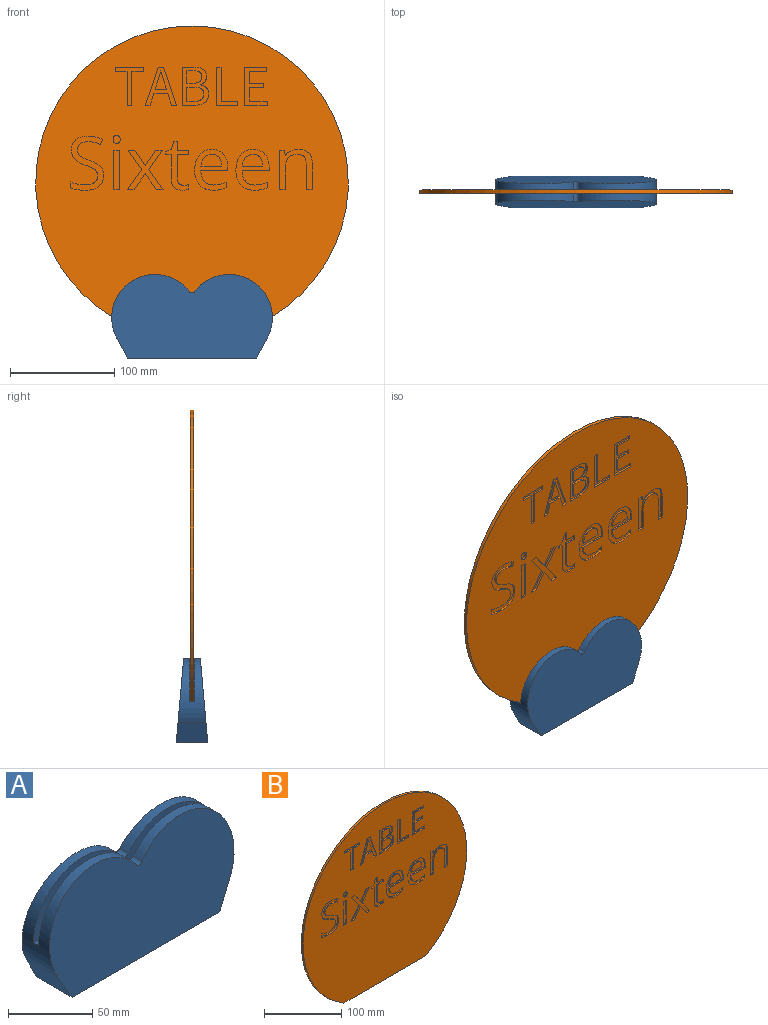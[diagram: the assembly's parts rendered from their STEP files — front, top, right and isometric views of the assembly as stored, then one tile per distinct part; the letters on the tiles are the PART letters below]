
ASSEMBLY  parts=2 mates=1
PART A: 67 faces, bbox 154.2x30x80.1 mm
  f0: plane 101.83x38.65mm, normal (0,-1,0), area 2079.1mm2, adj f5,f6,f9,f22,f25,f36,f37,f39
  f1: plane 101.83x38.65mm, normal (0,1,0), area 2079.1mm2, adj f2,f5,f6,f7,f21,f24,f26,f37
  f2: plane 14x1.74mm, normal (-1,0,0), area 24.3mm2, adj f1,f3,f38,f46
  f3: plane 16.17x14mm, normal (0,1,0), area 226.4mm2, adj f2,f38,f46,f61
  f4: plane 14x13.34mm, normal (0,-1,0), area 186.7mm2, adj f39,f40,f60,f62
  f5: plane 123.75x30mm, normal (0,0,-1), area 1755.7mm2, adj f0,f1,f12,f15,f16,f17,f23,f26
  f6: plane 35.45x10.65mm, normal (1,0,0), area 364.4mm2, adj f0,f1,f20,f21,f22,f24,f25,f37
  f7: plane 23.8x0.56mm, normal (-1,0,0), area 13.4mm2, adj f1,f24,f37,f55
  f8: plane 45.65x23.8mm, normal (0,1,0), area 1086.5mm2, adj f24,f37,f54,f55
  f9: plane 23.8x0.56mm, normal (-1,0,0), area 13.4mm2, adj f0,f25,f37,f53
  f10: plane 45.65x23.8mm, normal (0,-1,0), area 1086.5mm2, adj f25,f37,f52,f53
  f11: plane 24.61x4mm, normal (0,0,1), area 98.3mm2, adj f13,f18,f19,f23,f63,f64
  f12: plane 30x18.92mm, normal (0.88,0,-0.48), area 609.5mm2, adj f5,f13,f16,f17
  f13: cylinder r=41.5mm len=74.56mm, axis (0,1,0), area 1962.3mm2, adj f11,f12,f16,f17,f18,f19,f65,f66
  f14: cylinder r=41.5mm len=74.56mm, axis (0,1,0), area 1962.3mm2, adj f15,f16,f17,f18,f19,f20,f65,f66
  f15: plane 30x18.92mm, normal (-0.88,0,-0.48), area 609.5mm2, adj f5,f14,f16,f17
  f16: plane 154.17x80.15mm, normal (0,-1,0.09), area 10797.1mm2, adj f5,f12,f13,f14,f15,f66
  f17: plane 154.17x80.15mm, normal (0,1,0.09), area 10797.1mm2, adj f5,f12,f13,f14,f15,f65
  f18: plane 154.17x41.5mm, normal (0,1,0), area 5244.2mm2, adj f11,f13,f14,f20,f21,f66
  f19: plane 154.17x41.5mm, normal (0,-1,0), area 5244.2mm2, adj f11,f13,f14,f20,f22,f65
  f20: plane 24.58x4mm, normal (0,0,1), area 98.3mm2, adj f6,f14,f18,f19
  f21: plane 104.97x2.76mm, normal (0,0,-1), area 287.9mm2, adj f1,f6,f18,f64
  f22: plane 104.97x2.76mm, normal (0,0,-1), area 287.9mm2, adj f0,f6,f19,f63
  f23: plane 38.65x3.18mm, normal (-1,0,0), area 122.7mm2, adj f5,f11,f63,f64
  f24: plane 52x3.74mm, normal (0,0,-1), area 190mm2, adj f1,f6,f7,f8,f54,f55
  f25: plane 52x3.74mm, normal (0,0,-1), area 190mm2, adj f0,f6,f9,f10,f52,f53
  f26: extruded ~3.2x0.47mm, area 1.6mm2, adj f1,f5,f27,f37
  f27: plane 3.2x3.09mm, normal (-1,0,0), area 9.9mm2, adj f5,f26,f37,f48
  f28: plane 51.65x3.2mm, normal (0,1,0), area 165.3mm2, adj f5,f37,f48,f49
  f29: plane 3.2x3.09mm, normal (1,0,0), area 9.9mm2, adj f5,f30,f37,f49
  f30: extruded ~3.2x2.74mm, area 13mm2, adj f5,f29,f31,f37
  f31: cylinder r=2.5mm len=5mm, axis (0,0,-1), area 25.1mm2, adj f5,f30,f32,f37
  f32: extruded ~3.2x2.74mm, area 13mm2, adj f5,f31,f33,f37
  f33: plane 3.2x3.09mm, normal (1,0,0), area 9.9mm2, adj f5,f32,f37,f51
  f34: plane 51.65x3.2mm, normal (0,-1,0), area 165.3mm2, adj f5,f37,f50,f51
  f35: plane 3.2x3.09mm, normal (-1,0,0), area 9.9mm2, adj f5,f36,f37,f50
  f36: extruded ~3.2x0.47mm, area 1.6mm2, adj f0,f5,f35,f37
  f37: plane 63.11x23mm, normal (0,0,-1), area 447.2mm2, adj f0,f1,f6,f7,f8,f9,f10,f26
  f38: plane 19x1.74mm, normal (0,0,-1), area 31.6mm2, adj f1,f2,f3,f61
  f39: plane 19x1.74mm, normal (0,0,-1), area 30.2mm2, adj f0,f4,f60,f62
  f40: plane 22x3.24mm, normal (0,0,-1), area 36.7mm2, adj f0,f4,f41,f42,f43,f57,f58,f60
  f41: plane 15.65x8mm, normal (0,-1,0), area 125.2mm2, adj f5,f40,f57,f58
  f42: plane 8x0.06mm, normal (-1,0,0), area 0.5mm2, adj f0,f5,f40,f57
  f43: plane 8x0.06mm, normal (1,0,0), area 0.5mm2, adj f0,f5,f40,f58
  f44: plane 8x0.06mm, normal (1,0,0), area 0.5mm2, adj f1,f5,f46,f59
  f45: plane 8x0.06mm, normal (-1,0,0), area 0.5mm2, adj f1,f5,f46,f56
  f46: plane 22x3.24mm, normal (0,0,-1), area 35.3mm2, adj f1,f2,f3,f44,f45,f47,f56,f59
  f47: plane 15.65x8mm, normal (0,1,0), area 125.2mm2, adj f5,f46,f56,f59
  f48: cylinder r=3.17mm len=3.2mm, axis (0,0,1), area 16mm2, adj f5,f27,f28,f37
  f49: cylinder r=3.17mm len=3.2mm, axis (0,0,-1), area 16mm2, adj f5,f28,f29,f37
  f50: cylinder r=3.17mm len=3.2mm, axis (0,0,-1), area 16mm2, adj f5,f34,f35,f37
  f51: cylinder r=3.17mm len=3.2mm, axis (0,0,1), area 16mm2, adj f5,f33,f34,f37
  f52: cylinder r=3.17mm len=23.8mm, axis (0,0,1), area 118.7mm2, adj f6,f10,f25,f37
  f53: cylinder r=3.17mm len=23.8mm, axis (0,0,1), area 118.7mm2, adj f9,f10,f25,f37
  f54: cylinder r=3.17mm len=23.8mm, axis (0,0,-1), area 118.7mm2, adj f6,f8,f24,f37
  f55: cylinder r=3.17mm len=23.8mm, axis (0,0,-1), area 118.7mm2, adj f7,f8,f24,f37
  f56: cylinder r=3.17mm len=8mm, axis (0,0,1), area 39.9mm2, adj f5,f45,f46,f47
  f57: cylinder r=3.17mm len=8mm, axis (0,0,-1), area 39.9mm2, adj f5,f40,f41,f42
  f58: cylinder r=3.17mm len=8mm, axis (0,0,1), area 39.9mm2, adj f5,f40,f41,f43
  f59: cylinder r=3.17mm len=8mm, axis (0,0,-1), area 39.9mm2, adj f5,f44,f46,f47
  f60: cylinder r=3.17mm len=14mm, axis (0,0,-1), area 48.9mm2, adj f0,f4,f39,f40
  f61: cylinder r=3.17mm len=14mm, axis (0,0,-1), area 48.9mm2, adj f1,f3,f38,f46
  f62: cylinder r=3.17mm len=14mm, axis (0,0,-1), area 48.9mm2, adj f0,f4,f39,f40
  f63: cylinder r=3.17mm len=38.65mm, axis (0,0,-1), area 192.7mm2, adj f0,f5,f11,f22,f23
  f64: cylinder r=3.17mm len=38.65mm, axis (0,0,1), area 192.7mm2, adj f1,f5,f11,f21,f23
  f65: cylinder r=3.17mm len=7.53mm, axis (0,-1,0), area 43.9mm2, adj f13,f14,f17,f19
  f66: cylinder r=3.17mm len=7.53mm, axis (0,-1,0), area 43.9mm2, adj f13,f14,f16,f18
PART B: 203 faces, bbox 300x3.2x279.9 mm
  f0: plane 300x279.9mm, normal (0,-1,0), area 62829.4mm2, adj f1,f3,f4,f5,f6,f7,f8,f9
  f1: cylinder r=150mm len=300mm, axis (0,1,0), area 2493.6mm2, adj f0,f2,f3
  f2: plane 300x279.9mm, normal (0,1,0), area 68647.6mm2, adj f1,f3
  f3: plane 150x3.18mm, normal (0,0,-1), area 476.2mm2, adj f0,f1,f2
  f4: plane 32.8x2mm, normal (1,0,0), area 65.6mm2, adj f0,f5,f11,f12
  f5: plane 4.66x2mm, normal (0,0,1), area 9.3mm2, adj f0,f4,f6,f12
  f6: plane 32.8x2mm, normal (-1,0,0), area 65.6mm2, adj f0,f5,f7,f12
  f7: plane 11.12x2mm, normal (0,0,1), area 22.2mm2, adj f0,f6,f8,f12
  f8: plane 3.9x2mm, normal (-1,0,0), area 7.8mm2, adj f0,f7,f9,f12
  f9: plane 26.9x2mm, normal (0,0,-1), area 53.8mm2, adj f0,f8,f10,f12
  f10: plane 3.9x2mm, normal (1,0,0), area 7.8mm2, adj f0,f9,f11,f12
  f11: plane 11.12x2mm, normal (0,0,1), area 22.2mm2, adj f0,f4,f10,f12
  f12: plane 36.71x26.9mm, normal (0,-1,0), area 257.7mm2, adj f4,f5,f6,f7,f8,f9,f10,f11
  f13: plane 11.12x2mm, normal (0,0,-1), area 22.2mm2, adj f14,f26,f27,f200
  f14: plane 5.61x2mm, normal (-0.95,0,0.31), area 11.8mm2, adj f13,f15,f27,f200
  f15: extruded ~12.42x3.65mm, area 25.9mm2, adj f14,f16,f27,f200
  f16: plane 2x0.2mm, normal (0,0,1), area 0.4mm2, adj f15,f17,f27,f200
  f17: extruded ~12.42x3.7mm, area 25.9mm2, adj f16,f26,f27,f200
  f18: plane 11.22x3.51mm, normal (0.95,0,0.3), area 23.5mm2, adj f0,f19,f25,f27
  f19: plane 4.91x2mm, normal (0,0,1), area 9.8mm2, adj f0,f18,f20,f27
  f20: plane 36.71x12.47mm, normal (-0.95,0,-0.32), area 77.5mm2, adj f0,f19,f21,f27
  f21: plane 5.16x2mm, normal (0,0,-1), area 10.3mm2, adj f0,f20,f22,f27
  f22: plane 36.71x12.47mm, normal (0.95,0,-0.32), area 77.5mm2, adj f0,f21,f23,f27
  f23: plane 4.71x2mm, normal (0,0,1), area 9.4mm2, adj f0,f22,f24,f27
  f24: plane 11.22x3.55mm, normal (-0.95,0,0.3), area 23.5mm2, adj f0,f23,f25,f27
  f25: plane 13.42x2mm, normal (0,0,1), area 26.8mm2, adj f0,f18,f24,f27
  f26: plane 5.61x2mm, normal (0.95,0,0.3), area 11.8mm2, adj f13,f17,f27,f200
  f27: plane 36.71x30.1mm, normal (0,-1,0), area 357.5mm2, adj f13,f14,f15,f16,f17,f18,f19,f20
  f28: extruded ~7.25x2.96mm, area 16.2mm2, adj f29,f46,f47,f201
  f29: extruded ~6.9x2.88mm, area 15.5mm2, adj f28,f30,f47,f201
  f30: extruded ~8.29x2.41mm, area 17.6mm2, adj f29,f31,f47,f201
  f31: plane 19.76x2mm, normal (0,0,-1), area 39.5mm2, adj f30,f46,f47,f201
  f32: extruded ~13.22x5.11mm, area 29.2mm2, adj f0,f33,f45,f47
  f33: extruded ~6.53x2mm, area 13.1mm2, adj f0,f32,f34,f47
  f34: extruded ~5.74x2mm, area 12.1mm2, adj f0,f33,f35,f47
  f35: plane 5.11x2mm, normal (-1,0,0), area 10.2mm2, adj f0,f34,f36,f47
  f36: extruded ~12.06x2.55mm, area 24.8mm2, adj f0,f35,f37,f47
  f37: extruded ~8.98x3.45mm, area 19.8mm2, adj f0,f36,f38,f47
  f38: extruded ~10.1x3.37mm, area 21.8mm2, adj f0,f37,f39,f47
  f39: plane 26.03x2mm, normal (0,0,1), area 52.1mm2, adj f0,f38,f40,f47
  f40: plane 3.62x2mm, normal (-1,0,0), area 7.2mm2, adj f0,f39,f41,f47
  f41: extruded ~12.33x4.14mm, area 26.6mm2, adj f0,f40,f42,f47
  f42: extruded ~11.23x4.67mm, area 25.1mm2, adj f0,f41,f43,f47
  f43: extruded ~12.09x5.38mm, area 27.4mm2, adj f0,f42,f44,f47
  f44: extruded ~14.52x4.5mm, area 31.1mm2, adj f0,f43,f45,f47
  f45: extruded ~14.17x4.85mm, area 30.7mm2, adj f0,f32,f44,f47
  f46: extruded ~8.2x3.19mm, area 17.9mm2, adj f28,f31,f47,f201
  f47: plane 39.18x31.96mm, normal (0,-1,0), area 569.5mm2, adj f28,f29,f30,f31,f32,f33,f34,f35
  f48: extruded ~7.25x2.96mm, area 16.2mm2, adj f49,f66,f67,f202
  f49: extruded ~6.9x2.88mm, area 15.5mm2, adj f48,f50,f67,f202
  f50: extruded ~8.29x2.41mm, area 17.6mm2, adj f49,f51,f67,f202
  f51: plane 19.76x2mm, normal (0,0,-1), area 39.5mm2, adj f50,f66,f67,f202
  f52: extruded ~13.22x5.11mm, area 29.2mm2, adj f0,f53,f65,f67
  f53: extruded ~6.53x2mm, area 13.1mm2, adj f0,f52,f54,f67
  f54: extruded ~5.74x2mm, area 12.1mm2, adj f0,f53,f55,f67
  f55: plane 5.11x2mm, normal (-1,0,0), area 10.2mm2, adj f0,f54,f56,f67
  f56: extruded ~12.06x2.55mm, area 24.8mm2, adj f0,f55,f57,f67
  f57: extruded ~8.98x3.45mm, area 19.8mm2, adj f0,f56,f58,f67
  f58: extruded ~10.1x3.37mm, area 21.8mm2, adj f0,f57,f59,f67
  f59: plane 26.03x2mm, normal (0,0,1), area 52.1mm2, adj f0,f58,f60,f67
  f60: plane 3.62x2mm, normal (-1,0,0), area 7.2mm2, adj f0,f59,f61,f67
  f61: extruded ~12.33x4.14mm, area 26.6mm2, adj f0,f60,f62,f67
  f62: extruded ~11.23x4.67mm, area 25.1mm2, adj f0,f61,f63,f67
  f63: extruded ~12.09x5.38mm, area 27.4mm2, adj f0,f62,f64,f67
  f64: extruded ~14.52x4.5mm, area 31.1mm2, adj f0,f63,f65,f67
  f65: extruded ~14.17x4.85mm, area 30.7mm2, adj f0,f52,f64,f67
  f66: extruded ~8.2x3.19mm, area 17.9mm2, adj f48,f51,f67,f202
  f67: plane 39.18x31.96mm, normal (0,-1,0), area 569.5mm2, adj f48,f49,f50,f51,f52,f53,f54,f55
  f68: plane 36.71x2mm, normal (1,0,0), area 73.4mm2, adj f0,f69,f85,f86
  f69: plane 11.72x2mm, normal (0,0,1), area 23.4mm2, adj f0,f68,f70,f86
  f70: extruded ~13.92x10.77mm, area 39.8mm2, adj f0,f69,f71,f86
  f71: extruded ~8.76x7.51mm, area 25.3mm2, adj f0,f70,f72,f86
  f72: plane 2x0.25mm, normal (-1,0,0), area 0.5mm2, adj f0,f71,f73,f86
  f73: extruded ~7.97x5.41mm, area 20.6mm2, adj f0,f72,f74,f86
  f74: extruded ~12.62x8.96mm, area 35.1mm2, adj f0,f73,f85,f86
  f75: plane 6.41x2mm, normal (0,0,-1), area 12.8mm2, adj f76,f83,f86,f88
  f76: plane 13.82x2mm, normal (-1,0,0), area 27.6mm2, adj f75,f77,f86,f88
  f77: plane 6.41x2mm, normal (0,0,1), area 12.8mm2, adj f76,f78,f86,f88
  f78: extruded ~10.02x6.61mm, area 27.2mm2, adj f77,f83,f86,f88
  f79: plane 5.46x2mm, normal (0,0,-1), area 10.9mm2, adj f80,f84,f86,f87
  f80: plane 11.97x2mm, normal (-1,0,0), area 23.9mm2, adj f79,f81,f86,f87
  f81: plane 5.66x2mm, normal (0,0,1), area 11.3mm2, adj f80,f82,f86,f87
  f82: extruded ~8.67x5.91mm, area 24mm2, adj f81,f84,f86,f87
  f83: extruded ~10.02x7.21mm, area 28mm2, adj f75,f78,f86,f88
  f84: extruded ~8.87x6.06mm, area 24.4mm2, adj f79,f82,f86,f87
  f85: plane 10.92x2mm, normal (0,0,-1), area 21.8mm2, adj f0,f68,f74,f86
  f86: plane 36.71x25.64mm, normal (0,-1,0), area 472.9mm2, adj f68,f69,f70,f71,f72,f73,f74,f75
  f87: plane 14.33x11.97mm, normal (0,-1,0), area 154.5mm2, adj f79,f80,f81,f82,f84
  f88: plane 16.43x13.82mm, normal (0,-1,0), area 203.7mm2, adj f75,f76,f77,f78,f83
  f89: plane 36.71x2mm, normal (1,0,0), area 73.4mm2, adj f0,f90,f94,f95
  f90: plane 20.68x2mm, normal (0,0,1), area 41.4mm2, adj f0,f89,f91,f95
  f91: plane 3.96x2mm, normal (-1,0,0), area 7.9mm2, adj f0,f90,f92,f95
  f92: plane 16.03x2mm, normal (0,0,-1), area 32.1mm2, adj f0,f91,f93,f95
  f93: plane 32.75x2mm, normal (-1,0,0), area 65.5mm2, adj f0,f92,f94,f95
  f94: plane 4.66x2mm, normal (0,0,-1), area 9.3mm2, adj f0,f89,f93,f95
  f95: plane 36.71x20.68mm, normal (0,-1,0), area 234.4mm2, adj f89,f90,f91,f92,f93,f94
  f96: plane 36.71x2mm, normal (1,0,0), area 73.4mm2, adj f0,f97,f107,f108
  f97: plane 21.74x2mm, normal (0,0,1), area 43.5mm2, adj f0,f96,f98,f108
  f98: plane 3.96x2mm, normal (-1,0,0), area 7.9mm2, adj f0,f97,f99,f108
  f99: plane 17.08x2mm, normal (0,0,-1), area 34.2mm2, adj f0,f98,f100,f108
  f100: plane 13.37x2mm, normal (-1,0,0), area 26.7mm2, adj f0,f99,f101,f108
  f101: plane 13.92x2mm, normal (0,0,1), area 27.8mm2, adj f0,f100,f102,f108
  f102: plane 3.96x2mm, normal (-1,0,0), area 7.9mm2, adj f0,f101,f103,f108
  f103: plane 13.92x2mm, normal (0,0,-1), area 27.8mm2, adj f0,f102,f104,f108
  f104: plane 11.52x2mm, normal (-1,0,0), area 23mm2, adj f0,f103,f105,f108
  f105: plane 16.53x2mm, normal (0,0,1), area 33.1mm2, adj f0,f104,f106,f108
  f106: plane 3.9x2mm, normal (-1,0,0), area 7.8mm2, adj f0,f105,f107,f108
  f107: plane 21.18x2mm, normal (0,0,-1), area 42.4mm2, adj f0,f96,f106,f108
  f108: plane 36.71x21.74mm, normal (0,-1,0), area 358.2mm2, adj f96,f97,f98,f99,f100,f101,f102,f103
  f109: extruded ~10.38x4.83mm, area 23.8mm2, adj f0,f110,f133,f134
  f110: extruded ~8.41x2.98mm, area 18.3mm2, adj f0,f109,f111,f134
  f111: extruded ~10.91x6.07mm, area 25.2mm2, adj f0,f110,f112,f134
  f112: extruded ~7.02x3.08mm, area 15.4mm2, adj f0,f111,f113,f134
  f113: extruded ~3.26x3.07mm, area 9.1mm2, adj f0,f112,f114,f134
  f114: extruded ~4.29x2mm, area 8.9mm2, adj f0,f113,f115,f134
  f115: extruded ~5.55x2.62mm, area 12.8mm2, adj f0,f114,f116,f134
  f116: extruded ~7.28x2mm, area 15.4mm2, adj f0,f115,f117,f134
  f117: extruded ~12.14x2.61mm, area 25mm2, adj f0,f116,f118,f134
  f118: plane 5.1x2mm, normal (-0.94,0,0.34), area 10.8mm2, adj f0,f117,f119,f134
  f119: extruded ~13.82x2.76mm, area 28.4mm2, adj f0,f118,f120,f134
  f120: extruded ~11.59x3.45mm, area 24.6mm2, adj f0,f119,f121,f134
  f121: extruded ~9.27x4.37mm, area 21.3mm2, adj f0,f120,f122,f134
  f122: extruded ~9x3.02mm, area 19.4mm2, adj f0,f121,f123,f134
  f123: extruded ~10.05x5.96mm, area 23.6mm2, adj f0,f122,f124,f134
  f124: extruded ~7.5x3.21mm, area 16.3mm2, adj f0,f123,f125,f134
  f125: extruded ~3.52x3.09mm, area 9.5mm2, adj f0,f124,f126,f134
  f126: extruded ~4.29x2mm, area 8.9mm2, adj f0,f125,f127,f134
  f127: extruded ~6.19x2.97mm, area 14.3mm2, adj f0,f126,f128,f134
  f128: extruded ~8.83x2.22mm, area 18.5mm2, adj f0,f127,f129,f134
  f129: extruded ~7.24x2mm, area 14.6mm2, adj f0,f128,f130,f134
  f130: extruded ~6.76x2.06mm, area 14.2mm2, adj f0,f129,f131,f134
  f131: plane 5.65x2mm, normal (1,0,0), area 11.3mm2, adj f0,f130,f132,f134
  f132: extruded ~13.79x2.32mm, area 28.2mm2, adj f0,f131,f133,f134
  f133: extruded ~13.1x3.73mm, area 27.7mm2, adj f0,f109,f132,f134
  f134: plane 51.82x31.72mm, normal (0,-1,0), area 588.1mm2, adj f109,f110,f111,f112,f113,f114,f115,f116
  f135: plane 5.73x2mm, normal (0,0,1), area 11.5mm2, adj f0,f136,f138,f139
  f136: plane 37.79x2mm, normal (-1,0,0), area 75.6mm2, adj f0,f135,f137,f139
  f137: plane 5.73x2mm, normal (0,0,-1), area 11.5mm2, adj f0,f136,f138,f139
  f138: plane 37.79x2mm, normal (1,0,0), area 75.6mm2, adj f0,f135,f137,f139
  f139: plane 37.79x5.73mm, normal (0,-1,0), area 216.4mm2, adj f135,f136,f137,f138
  f140: extruded ~2.88x2mm, area 6.2mm2, adj f0,f141,f147,f148
  f141: extruded ~2.88x2mm, area 6.2mm2, adj f0,f140,f142,f148
  f142: extruded ~2.42x2mm, area 5.3mm2, adj f0,f141,f143,f148
  f143: extruded ~2.38x2mm, area 5.3mm2, adj f0,f142,f144,f148
  f144: extruded ~2.88x2mm, area 6.3mm2, adj f0,f143,f145,f148
  f145: extruded ~2.86x2mm, area 6.2mm2, adj f0,f144,f146,f148
  f146: extruded ~2.38x2mm, area 5.2mm2, adj f0,f145,f147,f148
  f147: extruded ~2.42x2mm, area 5.3mm2, adj f0,f140,f146,f148
  f148: plane 7.62x6.76mm, normal (0,-1,0), area 42mm2, adj f140,f141,f142,f143,f144,f145,f146,f147
  f149: plane 18.45x13.14mm, normal (0.81,0,0.58), area 45.3mm2, adj f0,f150,f160,f161
  f150: plane 19.34x13.82mm, normal (0.81,0,-0.58), area 47.5mm2, adj f0,f149,f151,f161
  f151: plane 6.48x2mm, normal (0,0,1), area 13mm2, adj f0,f150,f152,f161
  f152: plane 15.31x10.69mm, normal (-0.82,0,0.57), area 37.4mm2, adj f0,f151,f153,f161
  f153: plane 15.31x10.59mm, normal (0.82,0,0.57), area 37.2mm2, adj f0,f152,f154,f161
  f154: plane 6.48x2mm, normal (0,0,1), area 13mm2, adj f0,f153,f155,f161
  f155: plane 19.34x13.82mm, normal (-0.81,0,-0.58), area 47.5mm2, adj f0,f154,f156,f161
  f156: plane 18.45x13.14mm, normal (-0.81,0,0.58), area 45.3mm2, adj f0,f155,f157,f161
  f157: plane 6.45x2mm, normal (0,0,-1), area 12.9mm2, adj f0,f156,f158,f161
  f158: plane 14.47x9.93mm, normal (0.82,0,-0.57), area 35.1mm2, adj f0,f157,f159,f161
  f159: plane 14.47x9.96mm, normal (-0.82,0,-0.57), area 35.1mm2, adj f0,f158,f160,f161
  f160: plane 6.52x2mm, normal (0,0,-1), area 13mm2, adj f0,f149,f159,f161
  f161: plane 37.79x34.23mm, normal (0,-1,0), area 451.7mm2, adj f149,f150,f151,f152,f153,f154,f155,f156
  f162: extruded ~2.93x2mm, area 5.9mm2, adj f0,f163,f180,f181
  f163: extruded ~4.45x2mm, area 9.9mm2, adj f0,f162,f164,f181
  f164: extruded ~5.24x2mm, area 11.2mm2, adj f0,f163,f165,f181
  f165: plane 22.24x2mm, normal (-1,0,0), area 44.5mm2, adj f0,f164,f166,f181
  f166: plane 10.97x2mm, normal (0,0,1), area 21.9mm2, adj f0,f165,f167,f181
  f167: plane 4.45x2mm, normal (-1,0,0), area 8.9mm2, adj f0,f166,f168,f181
  f168: plane 10.97x2mm, normal (0,0,-1), area 21.9mm2, adj f0,f167,f169,f181
  f169: plane 8.76x2mm, normal (-1,0,0), area 17.5mm2, adj f0,f168,f170,f181
  f170: plane 3.31x2mm, normal (0,0,-1), area 6.6mm2, adj f0,f169,f171,f181
  f171: plane 8.06x2.41mm, normal (0.96,0,-0.29), area 16.8mm2, adj f0,f170,f172,f181
  f172: plane 5.42x2.38mm, normal (0.4,0,-0.92), area 11.8mm2, adj f0,f171,f173,f181
  f173: plane 2.76x2mm, normal (1,0,0), area 5.5mm2, adj f0,f172,f174,f181
  f174: plane 5.42x2mm, normal (0,0,1), area 10.8mm2, adj f0,f173,f175,f181
  f175: plane 22.48x2mm, normal (1,0,0), area 45mm2, adj f0,f174,f176,f181
  f176: extruded ~11.55x10.96mm, area 36.5mm2, adj f0,f175,f177,f181
  f177: extruded ~3.27x2mm, area 6.6mm2, adj f0,f176,f178,f181
  f178: extruded ~2.74x2mm, area 5.7mm2, adj f0,f177,f179,f181
  f179: plane 4.38x2mm, normal (-1,0,0), area 8.8mm2, adj f0,f178,f180,f181
  f180: extruded ~2.24x2mm, area 4.6mm2, adj f0,f162,f179,f181
  f181: plane 47.24x22.37mm, normal (0,-1,0), area 369.4mm2, adj f162,f163,f164,f165,f166,f167,f168,f169
  f182: plane 24.45x2mm, normal (1,0,0), area 48.9mm2, adj f0,f183,f198,f199
  f183: plane 5.73x2mm, normal (0,0,1), area 11.5mm2, adj f0,f182,f184,f199
  f184: plane 24.65x2mm, normal (-1,0,0), area 49.3mm2, adj f0,f183,f185,f199
  f185: extruded ~10.54x3.45mm, area 22.8mm2, adj f0,f184,f186,f199
  f186: extruded ~10.28x3.29mm, area 22.1mm2, adj f0,f185,f187,f199
  f187: extruded ~7.07x2mm, area 14.6mm2, adj f0,f186,f188,f199
  f188: extruded ~4.94x4.33mm, area 13.3mm2, adj f0,f187,f189,f199
  f189: plane 2x0.28mm, normal (0,0,-1), area 0.6mm2, adj f0,f188,f190,f199
  f190: plane 5.17x2mm, normal (-0.98,0,-0.18), area 10.5mm2, adj f0,f189,f191,f199
  f191: plane 4.66x2mm, normal (0,0,-1), area 9.3mm2, adj f0,f190,f192,f199
  f192: plane 37.79x2mm, normal (1,0,0), area 75.6mm2, adj f0,f191,f193,f199
  f193: plane 5.73x2mm, normal (0,0,1), area 11.5mm2, adj f0,f192,f194,f199
  f194: plane 19.83x2mm, normal (-1,0,0), area 39.7mm2, adj f0,f193,f195,f199
  f195: extruded ~10.59x2.76mm, area 22.3mm2, adj f0,f194,f196,f199
  f196: extruded ~8.68x3.21mm, area 19.1mm2, adj f0,f195,f197,f199
  f197: extruded ~6.59x2.28mm, area 14.4mm2, adj f0,f196,f198,f199
  f198: extruded ~6.89x2.1mm, area 14.7mm2, adj f0,f182,f197,f199
  f199: plane 38.48x31.59mm, normal (0,-1,0), area 517.6mm2, adj f182,f183,f184,f185,f186,f187,f188,f189
  f200: plane 18.03x11.12mm, normal (0,-1,0), area 99.4mm2, adj f13,f14,f15,f16,f17,f26
  f201: plane 19.76x11.17mm, normal (0,-1,0), area 177.8mm2, adj f28,f29,f30,f31,f46
  f202: plane 19.76x11.17mm, normal (0,-1,0), area 177.8mm2, adj f48,f49,f50,f51,f66
PLACE A t=(0,0,-138)mm
PLACE B t=(-0.03,1.59,-8.1)mm
MATE fastened B.f3 <-> A.f20  axis (0,0,-1) through (-75.03,0,-138)mm
